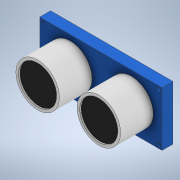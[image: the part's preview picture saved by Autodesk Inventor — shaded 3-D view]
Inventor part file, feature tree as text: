
AUTODESK INVENTOR PART (.ipt)
format: ipt  version: 2021 (Build 250183000, 183)  size: 162,304 bytes
history: native  units: mm
features: extrude x3, other x1, sketch x1
ambient origin geometry x8: Origin, YZ Plane, XZ Plane, XY Plane, X Axis, Y Axis, Z Axis, Center Point
bodies: Volumenkörper1 (feature_tree)
feature tree (5):
  other  "Ultraschallsensor"
  sketch  "Skizze1"  dims[d0=20.0mm d1=45.0mm d2=16.0mm d3=11.25mm d4=1.5mm d5=1.25mm d6=1.25mm d7=4.0mm d8=0.0mm d11=1.0mm d12=1.0mm d13=12.0mm d14=0.0mm d15=11.5mm d16=0.0mm]
  extrude  "Extrusion1"  Depth=45.0mm
  extrude  "Extrusion3"  Depth=16.0mm
  extrude  "Extrusion4"  Depth=11.25mm
